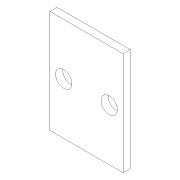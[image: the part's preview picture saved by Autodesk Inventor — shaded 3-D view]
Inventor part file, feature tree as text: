
AUTODESK INVENTOR PART (.ipt)
format: ipt  version: 2022 (Build 260153000, 153)  size: 92,160 bytes
history: native  units: mm
features: extrude x1, sketch x1
ambient origin geometry x8: Origin, YZ Plane, XZ Plane, XY Plane, X Axis, Y Axis, Z Axis, Center Point
bodies: Body1 (feature_tree)
feature tree (2):
  extrude  "Extrusion2"  Depth=14.5mm
  sketch  "Sketch1"  dims[d0=10.3mm d1=14.5mm d2=2.5mm d3=3.0mm d4=3.9mm d5=0.0mm d6=2.3mm d7=1.95mm d8=7.25mm d9=2.3mm d10=1.95mm d11=7.25mm d15=1.0mm d16=0.0mm]
